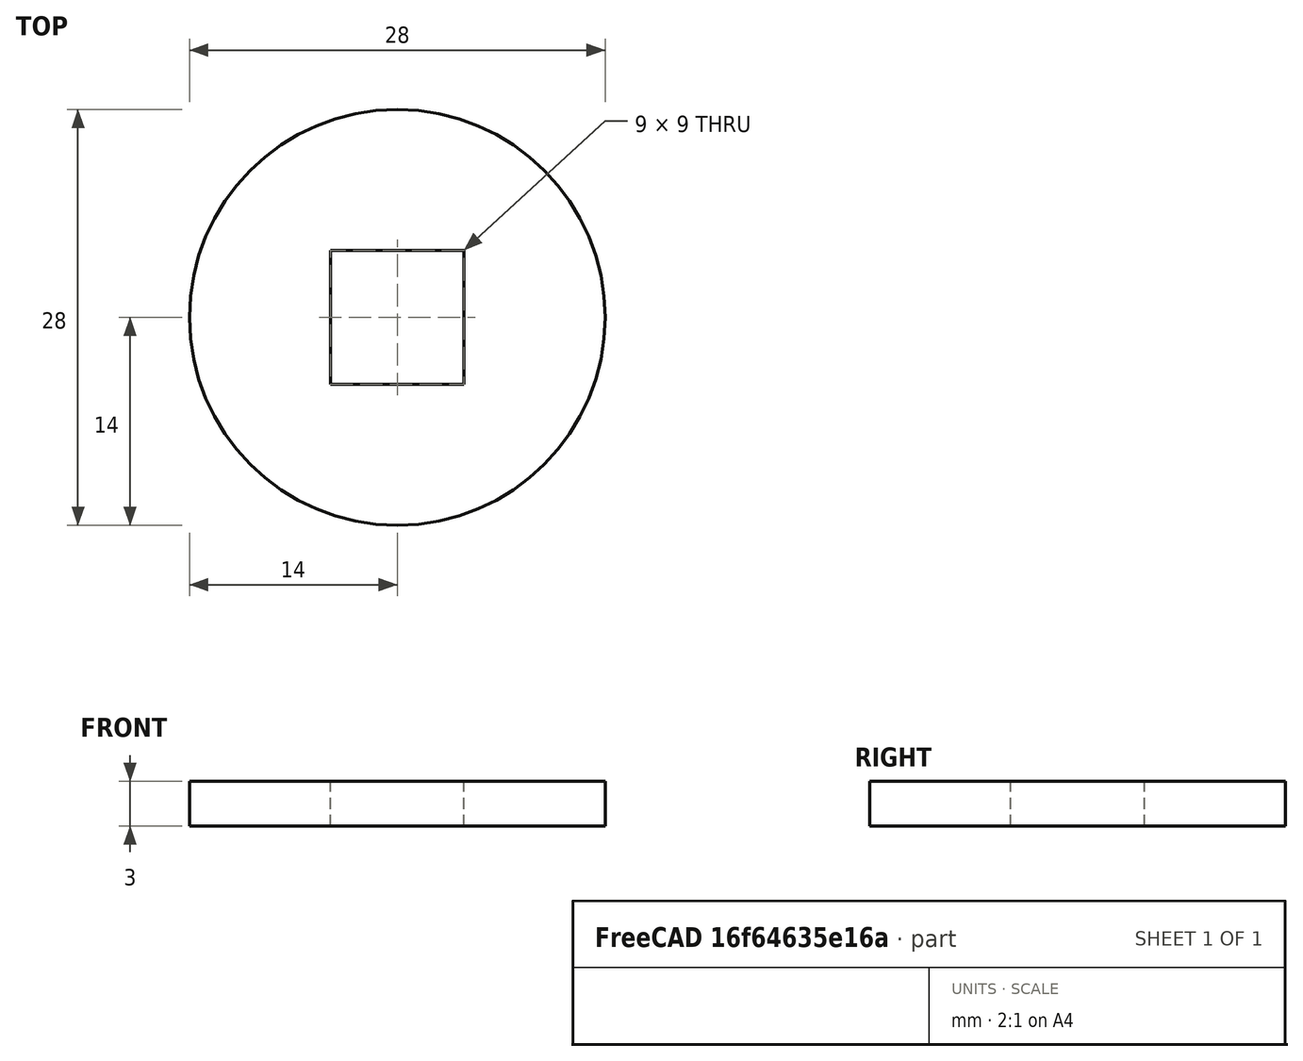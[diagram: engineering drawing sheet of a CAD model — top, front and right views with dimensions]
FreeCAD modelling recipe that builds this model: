
FCSTD DOCUMENT  (FreeCAD 0.15R4671 (Git))
Label: DIN440_CLASS_V_M8
License: CreativeCommons Attribution-ShareAlike
LicenseURL: http://creativecommons.org/licenses/by-sa/4.0/
objects: Sketcher::SketchObject×1, PartDesign::Pad×1
note: 3 computed .brp shape members not serialized (recipe doc carries the construction recipe); baked Part::Feature solids carry a one-line shape summary decoded from their .brp

FEATURE [Sketcher::SketchObject] Sketch
  sketch-geometry (5):
    g0: Circle CenterX=0 CenterY=0 CenterZ=0 NormalX=0 NormalY=0 NormalZ=1 Radius=14
    g1: LineSegment StartX=-4.5 StartY=4.5 StartZ=0 EndX=4.5 EndY=4.5 EndZ=0
    g2: LineSegment StartX=4.5 StartY=4.5 StartZ=0 EndX=4.5 EndY=-4.5 EndZ=0
    g3: LineSegment StartX=4.5 StartY=-4.5 StartZ=0 EndX=-4.5 EndY=-4.5 EndZ=0
    g4: LineSegment StartX=-4.5 StartY=-4.5 StartZ=0 EndX=-4.5 EndY=4.5 EndZ=0
  constraints (15):
    c: Coincident(g0,g-1)
    c: Radius(g0) = 14
    c: Coincident(g1,g2)
    c: Coincident(g2,g3)
    c: Coincident(g3,g4)
    c: Coincident(g4,g1)
    c: Horizontal(g1)
    c: Horizontal(g3)
    c: Vertical(g2)
    c: Vertical(g4)
    c: Equal(g1,g4)
    c: Equal(g4,g3)
    c: Equal(g3,g2)
    c: DistanceX(g1,g1) = 9
    c: Symmetric(g2,g1,g-1)
FEATURE [PartDesign::Pad] Pad
  Length = 3
  Length2 = 100
  Sketch = -> Sketch
  Type = 0
